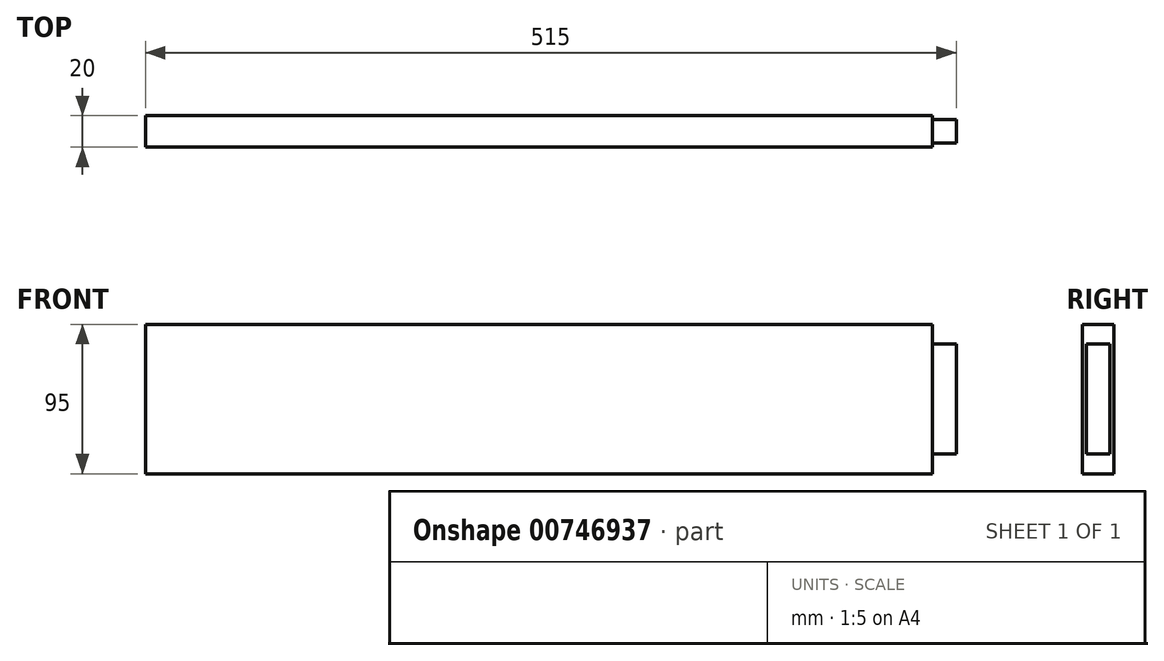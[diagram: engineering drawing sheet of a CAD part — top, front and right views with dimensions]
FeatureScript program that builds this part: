
annotation { "Feature Type Name" : "Feature", "Feature Type Description" : "" }
export const myFeature = defineFeature(function(context is Context, id is Id, definition is map)
    precondition{}
    {
        {
            var Q0;
            Q0=qCreatedBy(makeId("Right.planeOp"),FACE);
            var sketch = newSketch(context, id + "F0", { "sketchPlane" : qUnion([Q0])});
            skLineSegment(sketch, "E0.bottom", {"start": v(10, 47.5) * mm, "end": v(-10, 47.5) * mm});
            skLineSegment(sketch, "E0.top", {"start": v(10, -47.5) * mm, "end": v(-10, -47.5) * mm});
            skLineSegment(sketch, "E0.left", {"start": v(10, 47.5) * mm, "end": v(10, -47.5) * mm});
            skLineSegment(sketch, "E0.right", {"start": v(-10, 47.5) * mm, "end": v(-10, -47.5) * mm});
            skPoint(sketch, "E0.middle", {"position": v(0, 0) * mm});
            skSolve(sketch);
        }
        {
            var Q0;
            Q0 = qSketchRegion(id + "F0", true);
            extrude(context, id + "F1", {"entities" : qUnion([Q0]), "endBound" : BoundingType.SYMMETRIC, "depth" : 500 * mm, "offsetDistance" : 25 * mm});
        }
        {
            var Q0;
            Q0=makeQuery(id+"F1.opExtrude","CAP_FACE",FACE,{"disambiguationData":[OSD([sQuery(id+"F0.wireOp",EDGE,"E0.bottom"),sQuery(id+"F0.wireOp",EDGE,"E0.top"),sQuery(id+"F0.wireOp",EDGE,"E0.left"),sQuery(id+"F0.wireOp",EDGE,"E0.right")])],"isStart":false});
            var sketch = newSketch(context, id + "F2", { "sketchPlane" : qUnion([Q0])});
            skLineSegment(sketch, "E1.bottom", {"start": v(7.5, 35) * mm, "end": v(-7.5, 35) * mm});
            skLineSegment(sketch, "E1.top", {"start": v(7.5, -35) * mm, "end": v(-7.5, -35) * mm});
            skLineSegment(sketch, "E1.left", {"start": v(7.5, 35) * mm, "end": v(7.5, -35) * mm});
            skLineSegment(sketch, "E1.right", {"start": v(-7.5, 35) * mm, "end": v(-7.5, -35) * mm});
            skPoint(sketch, "E1.middle", {"position": v(0, 0) * mm});
            skSolve(sketch);
        }
        {
            var Q0;
            Q0 = qSketchRegion(id + "F2", true);
            extrude(context, id + "F3", {"entities" : qUnion([Q0]), "operationType" : NewBodyOperationType.ADD, "depth" : 15 * mm, "offsetDistance" : 25 * mm});
        }
    });
